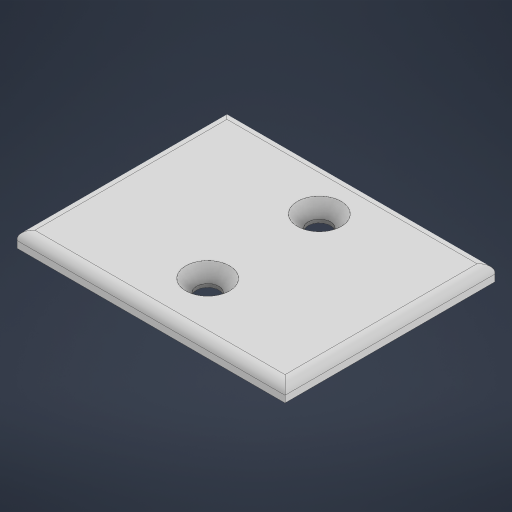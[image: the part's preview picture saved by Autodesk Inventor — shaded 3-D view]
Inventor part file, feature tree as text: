
AUTODESK INVENTOR PART (.ipt)
format: ipt  version: 2024 (Build 280153000, 153)  size: 195,072 bytes
history: native  units: in
note: dims shown in document units (in); Inventor stores cm internally (conversion verified against a paired STEP export)
features: sketch x2, extrude x1, hole x1, fillet x1
ambient origin geometry x8: Origin, YZ Plane, XZ Plane, XY Plane, X Axis, Y Axis, Z Axis, Center Point
bodies: Solid1 (feature_tree)
feature tree (5):
  extrude  "Extrusion1"  Depth=1.8504in
  hole  "Hole1"  [1 undecoded]
  fillet  "Fillet2"  Radius=0.4724in
  sketch  "Sketch1"  dims[d0=2.3622in d1=1.8504in]
  sketch  "Sketch2"  dims[d7=0.1378in d8=0.0in d10=0.9843in d11=0.4724in d12=0.3937in d13=0.196in d14=0.2362in d15=0.385in d16=0.0787in d17=0.5635in d18=0.315in d19=0.8108in d20=0.0787in]
note: 1 required parameter value undecoded (feature->parameter linkage not recoverable at this tier; creation-order binding heuristic only, values carry confidence <= 0.55)
